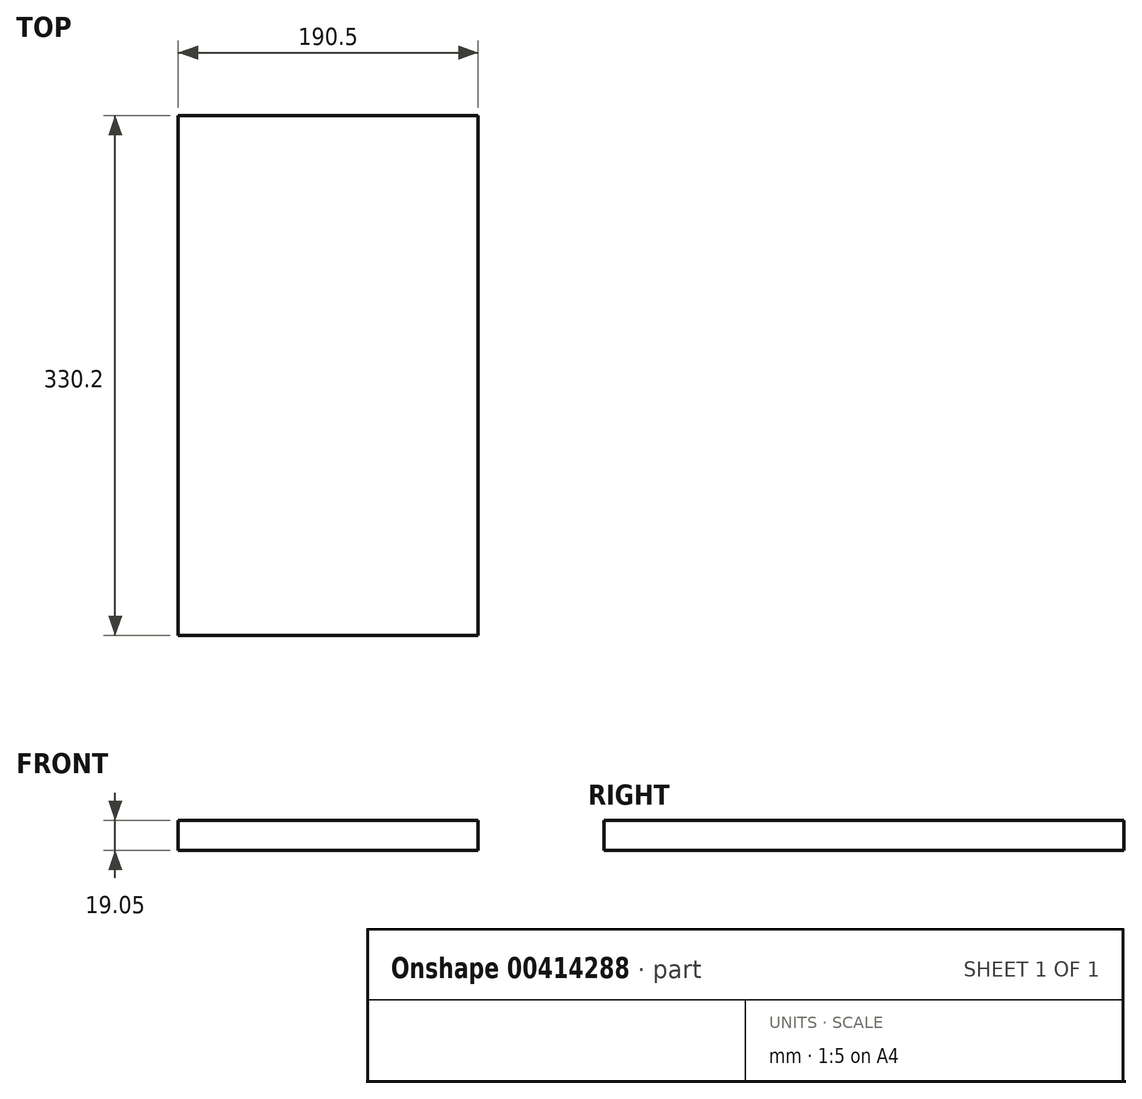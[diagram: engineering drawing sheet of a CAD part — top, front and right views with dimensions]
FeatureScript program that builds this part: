
annotation { "Feature Type Name" : "Feature", "Feature Type Description" : "" }
export const myFeature = defineFeature(function(context is Context, id is Id, definition is map)
    precondition{}
    {
        {
            var Q0;
            Q0=qCreatedBy(makeId("Front.planeOp"),FACE);
            var sketch = newSketch(context, id + "F0", { "sketchPlane" : qUnion([Q0])});
            skLineSegment(sketch, "E0.bottom", {"start": v(0, 0) * mm, "end": v(-190.5, 0) * mm});
            skLineSegment(sketch, "E0.top", {"start": v(0, 19.05) * mm, "end": v(-190.5, 19.05) * mm});
            skLineSegment(sketch, "E0.left", {"start": v(0, 0) * mm, "end": v(0, 19.05) * mm});
            skLineSegment(sketch, "E0.right", {"start": v(-190.5, 0) * mm, "end": v(-190.5, 19.05) * mm});
            skSolve(sketch);
        }
        {
            var Q0;
            Q0=qSketchRegion(id+"F0",true);
            extrude(context, id + "F1", {"entities" : qUnion([Q0]), "depth" : 330.2 * mm});
        }
    });
